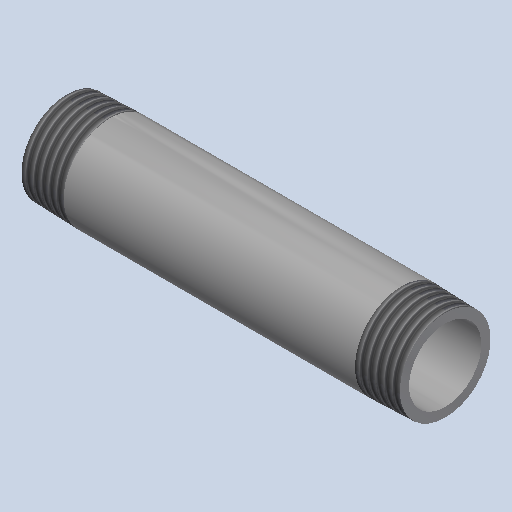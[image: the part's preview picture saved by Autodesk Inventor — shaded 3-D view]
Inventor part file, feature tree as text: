
AUTODESK INVENTOR PART (.ipt)
format: ipt  version: 2025 (Build 290162000, 162)  size: 217,088 bytes
history: native  units: mm (DEFAULTED — no unit token found)
features: other x8, revolve x1
ambient origin geometry x8: Origin, YZ Plane, XZ Plane, XY Plane, X Axis, Y Axis, Z Axis, Center Point
bodies: Solid1 (feature_tree)
feature tree (9):
  revolve  "Revolution1"  [1 undecoded]
  other  "Work Axis1"
  other  "Work Point5"
  other  "Work Axis2"
  other  "Work Point6"
  other  "Work Axis3"
  other  "Work Axis4"
  other  "Work Point7"
  other  "Work Point8"
note: 1 required parameter value undecoded (feature->parameter linkage not recoverable at this tier; creation-order binding heuristic only, values carry confidence <= 0.55)
